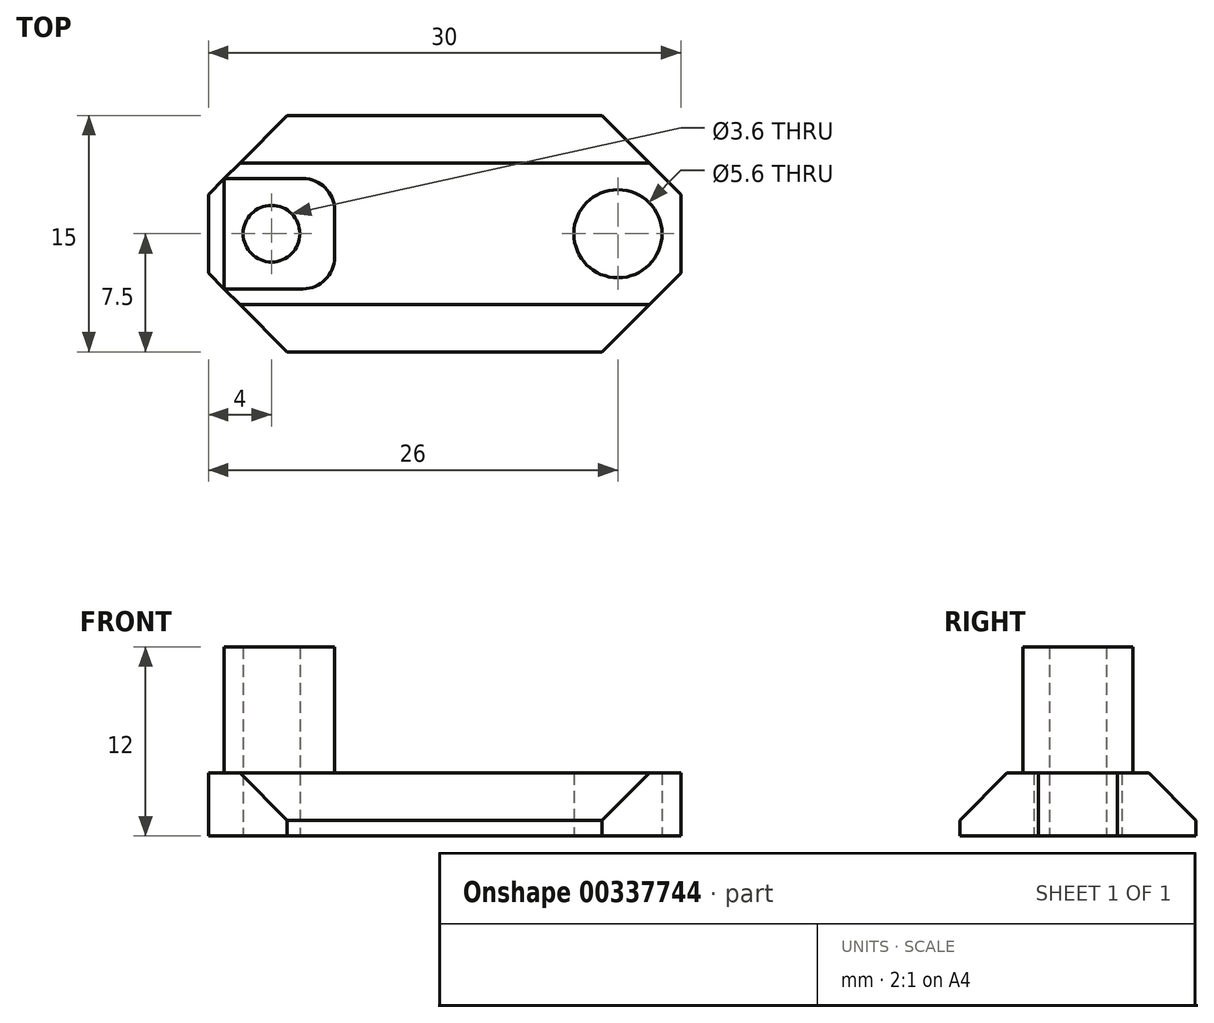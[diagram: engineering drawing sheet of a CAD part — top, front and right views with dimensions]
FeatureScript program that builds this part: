
annotation { "Feature Type Name" : "Feature", "Feature Type Description" : "" }
export const myFeature = defineFeature(function(context is Context, id is Id, definition is map)
    precondition{}
    {
        {
            var Q0;
            Q0=qCreatedBy(makeId("Top.planeOp"),FACE);
            var sketch = newSketch(context, id + "F0", { "sketchPlane" : qUnion([Q0])});
            skLineSegment(sketch, "E0.bottom", {"start": v(15, 7.5) * mm, "end": v(-15, 7.5) * mm});
            skLineSegment(sketch, "E0.top", {"start": v(15, -7.5) * mm, "end": v(-15, -7.5) * mm});
            skLineSegment(sketch, "E0.left", {"start": v(15, 7.5) * mm, "end": v(15, -7.5) * mm});
            skLineSegment(sketch, "E0.right", {"start": v(-15, 7.5) * mm, "end": v(-15, -7.5) * mm});
            skPoint(sketch, "E0.middle", {"position": v(0, 0) * mm});
            skLineSegment(sketch, "E1", {"start": v(15, 0) * mm, "end": v(11, 0) * mm});
            skLineSegment(sketch, "E2", {"start": v(-15, 0) * mm, "end": v(-11, 0) * mm});
            skPoint(sketch, "E2.endSnap0", {"position": v(-15, 0) * mm});
            skCircle(sketch, "E3", {"center": v(-11, 0) * mm, "radius": 1.8 * mm});
            skCircle(sketch, "E4", {"center": v(11, 0) * mm, "radius": 2.8 * mm});
            skLineSegment(sketch, "E5", {"start": v(-15, 7.5) * mm, "end": v(-5, 7.5) * mm});
            skLineSegment(sketch, "E6", {"start": v(-5, 7.5) * mm, "end": v(0, 0) * mm});
            skLineSegment(sketch, "E7", {"start": v(15, 7.5) * mm, "end": v(5, 7.5) * mm});
            skLineSegment(sketch, "E8", {"start": v(5, 7.5) * mm, "end": v(0, 0) * mm});
            skLineSegment(sketch, "E9", {"start": v(0, 0) * mm, "end": v(0, 3.75) * mm});
            skPoint(sketch, "E9.endSnap0", {"position": v(-2.5, 3.75) * mm});
            skLineSegment(sketch, "E10", {"start": v(0, 3.75) * mm, "end": v(2.5, 3.75) * mm});
            skLineSegment(sketch, "E11", {"start": v(2.5, 3.75) * mm, "end": v(-2.5, 3.75) * mm});
            skLineSegment(sketch, "E12", {"start": v(-15, -7.5) * mm, "end": v(-5, -7.5) * mm});
            skLineSegment(sketch, "E13", {"start": v(15, -7.5) * mm, "end": v(5, -7.5) * mm});
            skLineSegment(sketch, "E14", {"start": v(5, -7.5) * mm, "end": v(0, 0) * mm});
            skLineSegment(sketch, "E15", {"start": v(-5, -7.5) * mm, "end": v(0, 0) * mm});
            skLineSegment(sketch, "E16", {"start": v(0, 0) * mm, "end": v(0, -3.75) * mm});
            skLineSegment(sketch, "E17", {"start": v(0, -3.75) * mm, "end": v(2.5, -3.75) * mm});
            skLineSegment(sketch, "E18", {"start": v(2.5, -3.75) * mm, "end": v(-2.5, -3.75) * mm});
            skSolve(sketch);
        }
        {
            var Q0;
            Q0=makeQuery(id+"F0.imprint","IMPRINT",FACE,{"disambiguationData":[TD([[makeQuery(id+"F0.imprint","IMPRINT",EDGE,{"derivedFrom":sQuery(id+"F0.wireOp",EDGE,"E3")}),-1.0]])]});
            var Q1;
            Q1=makeQuery(id+"F0.imprint","IMPRINT",FACE,{"disambiguationData":[TD([[makeQuery(id+"F0.imprint","IMPRINT",EDGE,{"derivedFrom":sQuery(id+"F0.wireOp",EDGE,"E4")}),-1.0]])]});
            var Q2;
            {var subQ0=sQuery(id+"F0.wireOp",EDGE,"E9");Q2=makeQuery(id+"F0.imprint","IMPRINT",FACE,{"disambiguationData":[TD([[makeQuery(id+"F0.imprint","IMPRINT",EDGE,{"derivedFrom":subQ0}),-1.0]])]});}
            var Q3;
            {var subQ0=sQuery(id+"F0.wireOp",EDGE,"E9");Q3=makeQuery(id+"F0.imprint","IMPRINT",FACE,{"disambiguationData":[TD([[makeQuery(id+"F0.imprint","IMPRINT",EDGE,{"derivedFrom":subQ0}),1.0]])]});}
            var Q4;
            {var subQ0=sQuery(id+"F0.wireOp",EDGE,"E16");Q4=makeQuery(id+"F0.imprint","IMPRINT",FACE,{"disambiguationData":[TD([[makeQuery(id+"F0.imprint","IMPRINT",EDGE,{"derivedFrom":subQ0}),-1.0]])]});}
            var Q5;
            {var subQ0=sQuery(id+"F0.wireOp",EDGE,"E16");Q5=makeQuery(id+"F0.imprint","IMPRINT",FACE,{"disambiguationData":[TD([[makeQuery(id+"F0.imprint","IMPRINT",EDGE,{"derivedFrom":subQ0}),1.0]])]});}
            var Q6;
            {var subQ4=sQuery(id+"F0.wireOp",EDGE,"E0.top");Q6=makeQuery(id+"F0.imprint","IMPRINT",FACE,{"disambiguationData":[TD([[makeQuery(id+"F0.imprint","IMPRINT",EDGE,{"derivedFrom":subQ4}),-1.0]])]});}
            var Q7;
            {var subQ1=sQuery(id+"F0.wireOp",EDGE,"E0.bottom");Q7=makeQuery(id+"F0.imprint","IMPRINT",FACE,{"disambiguationData":[TD([[makeQuery(id+"F0.imprint","IMPRINT",EDGE,{"derivedFrom":subQ1}),1.0]])]});}
            extrude(context, id + "F1", {"entities" : qUnion([Q0, Q1, Q2, Q3, Q4, Q5, Q6, Q7]), "depth" : 4 * mm});
        }
        {
            var Q0;
            Q0=makeQuery(id+"F1.opExtrude","SWEPT_EDGE",EDGE,{"disambiguationData":[OSD([sQuery(id+"F0.wireOp",EDGE,"E0.right"),sQuery(id+"F0.wireOp",EDGE,"E5")])]});
            var Q1;
            Q1=makeQuery(id+"F1.opExtrude","SWEPT_EDGE",EDGE,{"disambiguationData":[OSD([sQuery(id+"F0.wireOp",EDGE,"E0.right"),sQuery(id+"F0.wireOp",EDGE,"E12")])]});
            var Q2;
            Q2=makeQuery(id+"F1.opExtrude","SWEPT_EDGE",EDGE,{"disambiguationData":[OSD([sQuery(id+"F0.wireOp",EDGE,"E0.left"),sQuery(id+"F0.wireOp",EDGE,"E13")])]});
            var Q3;
            Q3=makeQuery(id+"F1.opExtrude","SWEPT_EDGE",EDGE,{"disambiguationData":[OSD([sQuery(id+"F0.wireOp",EDGE,"E0.left"),sQuery(id+"F0.wireOp",EDGE,"E7")])]});
            chamfer(context, id + "F2", {"entities" : qUnion([Q0, Q1, Q2, Q3]), "width" : 5 * mm, "tangentPropagation" : true});
        }
        {
            var Q0;
            Q0=makeQuery(id+"F1.opExtrude","CAP_EDGE",EDGE,{"disambiguationData":[OSD([sQuery(id+"F0.wireOp",EDGE,"E0.top"),sQuery(id+"F0.wireOp",EDGE,"E12"),sQuery(id+"F0.wireOp",EDGE,"E13")])],"isStart":false});
            var Q1;
            Q1=makeQuery(id+"F1.opExtrude","CAP_EDGE",EDGE,{"disambiguationData":[OSD([sQuery(id+"F0.wireOp",EDGE,"E0.bottom"),sQuery(id+"F0.wireOp",EDGE,"E5"),sQuery(id+"F0.wireOp",EDGE,"E7")])],"isStart":false});
            chamfer(context, id + "F3", {"entities" : qUnion([Q0, Q1]), "width" : 3 * mm, "tangentPropagation" : true});
        }
        {
            var Q0;
            Q0=makeQuery(id+"F1.opExtrude","CAP_FACE",FACE,{"disambiguationData":[OSD([sQuery(id+"F0.wireOp",EDGE,"E0.bottom"),sQuery(id+"F0.wireOp",EDGE,"E0.top"),sQuery(id+"F0.wireOp",EDGE,"E0.left"),sQuery(id+"F0.wireOp",EDGE,"E0.right"),sQuery(id+"F0.wireOp",EDGE,"E3"),sQuery(id+"F0.wireOp",EDGE,"E4"),sQuery(id+"F0.wireOp",EDGE,"E5"),sQuery(id+"F0.wireOp",EDGE,"E7"),sQuery(id+"F0.wireOp",EDGE,"E12"),sQuery(id+"F0.wireOp",EDGE,"E13")])],"isStart":false});
            var sketch = newSketch(context, id + "F4", { "sketchPlane" : qUnion([Q0])});
            skLineSegment(sketch, "E19", {"start": v(0, 0) * mm, "end": v(-7, 0) * mm});
            skLineSegment(sketch, "E20", {"start": v(-7, 0) * mm, "end": v(-7, -3.5) * mm});
            skLineSegment(sketch, "E21.bottom", {"start": v(-7, -3.5) * mm, "end": v(-14, -3.5) * mm});
            skLineSegment(sketch, "E21.top", {"start": v(-7, 3.5) * mm, "end": v(-14, 3.5) * mm});
            skLineSegment(sketch, "E21.left", {"start": v(-7, -3.5) * mm, "end": v(-7, 3.5) * mm});
            skLineSegment(sketch, "E21.right", {"start": v(-14, -3.5) * mm, "end": v(-14, 3.5) * mm});
            skSolve(sketch);
        }
        {
            var Q0;
            {var subQ3=sQuery(id+"F4.wireOp",EDGE,"E21.bottom");Q0=makeQuery(id+"F4.imprint","IMPRINT",FACE,{"disambiguationData":[TD([[makeQuery(id+"F4.imprint","IMPRINT",EDGE,{"derivedFrom":subQ3}),-1.0]])]});}
            extrude(context, id + "F5", {"entities" : qUnion([Q0]), "operationType" : NewBodyOperationType.ADD, "depth" : 8 * mm});
        }
        {
            var Q0;
            Q0=makeQuery(id+"F5.opExtrude","SWEPT_EDGE",EDGE,{"disambiguationData":[OSD([sQuery(id+"F4.wireOp",EDGE,"E21.top"),sQuery(id+"F4.wireOp",EDGE,"E21.left")])]});
            var Q1;
            Q1=makeQuery(id+"F5.opExtrude","SWEPT_EDGE",EDGE,{"disambiguationData":[OSD([sQuery(id+"F4.wireOp",EDGE,"E21.bottom"),sQuery(id+"F4.wireOp",EDGE,"E21.left")])]});
            fillet(context, id + "F6", {"entities" : qUnion([Q0, Q1]), "radius" : 2 * mm, "tangentPropagation" : true, "allowEdgeOverflow" : false});
        }
    });
